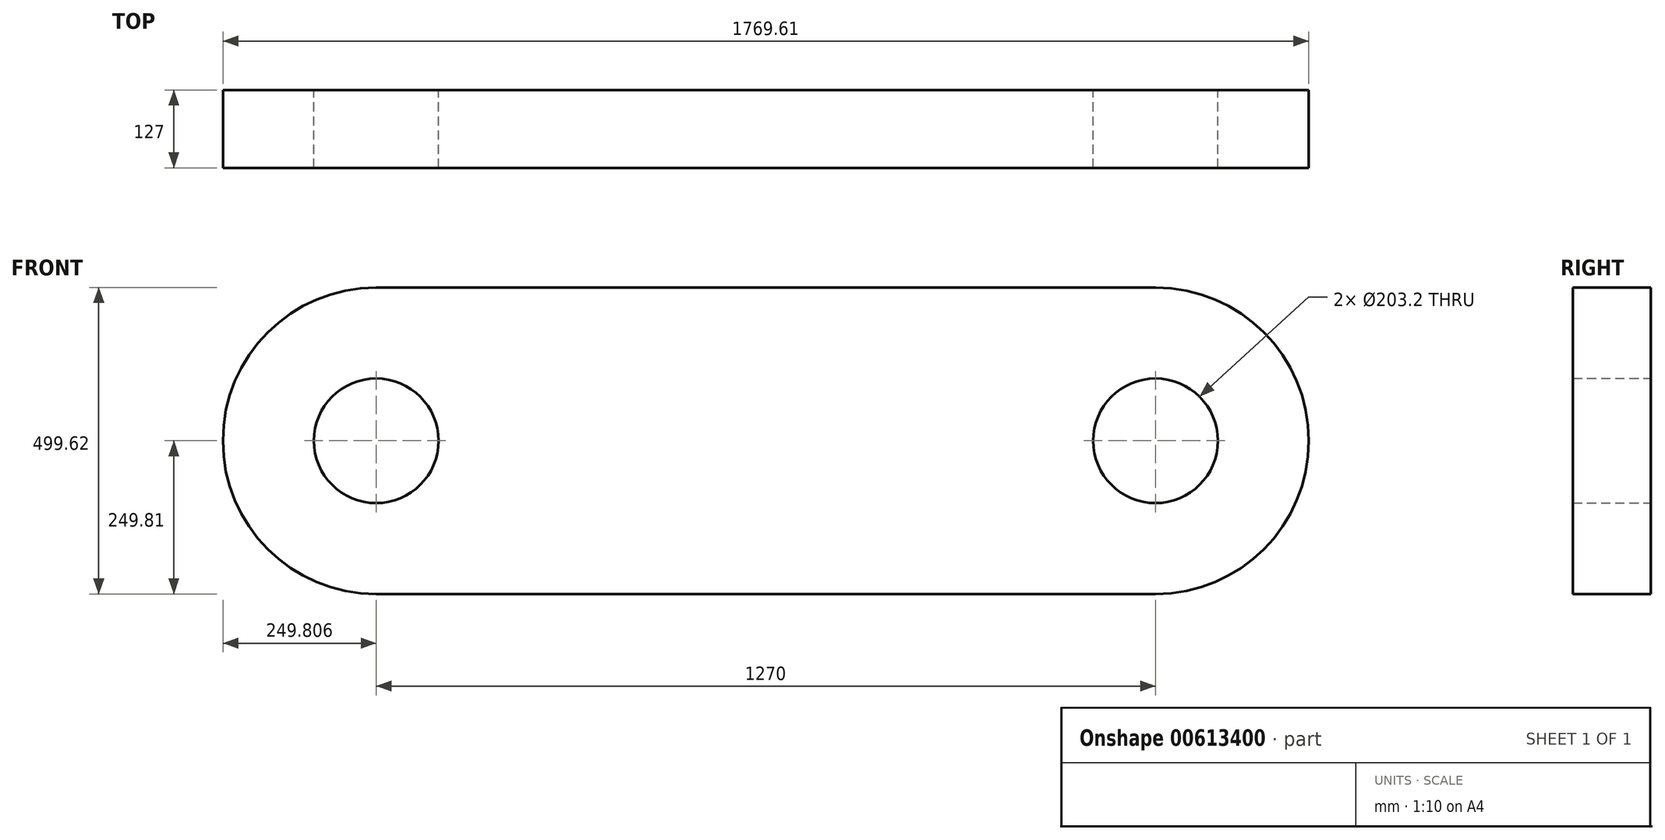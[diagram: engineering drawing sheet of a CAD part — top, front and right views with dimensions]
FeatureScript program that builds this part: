
annotation { "Feature Type Name" : "Feature", "Feature Type Description" : "" }
export const myFeature = defineFeature(function(context is Context, id is Id, definition is map)
    precondition{}
    {
        {
            var Q0;
            Q0=qCreatedBy(makeId("Front.planeOp"),FACE);
            var sketch = newSketch(context, id + "F0", { "sketchPlane" : qUnion([Q0])});
            skLineSegment(sketch, "E0", {"start": v(-559.22, 0) * mm, "end": v(710.78, 0) * mm});
            skCircle(sketch, "E1", {"center": v(-559.22, 0) * mm, "radius": 249.8 * mm});
            skCircle(sketch, "E2", {"center": v(710.78, 0) * mm, "radius": 249.8 * mm});
            skLineSegment(sketch, "E3", {"start": v(-559.22, 249.8) * mm, "end": v(710.78, 249.8) * mm});
            skLineSegment(sketch, "E4", {"start": v(-559.22, -249.8) * mm, "end": v(710.78, -249.8) * mm});
            skCircle(sketch, "E5", {"center": v(-559.22, 0) * mm, "radius": 101.6 * mm});
            skCircle(sketch, "E6", {"center": v(710.78, 0) * mm, "radius": 101.6 * mm});
            skSolve(sketch);
        }
        {
            var Q0;
            Q0=makeQuery(id+"F0.imprint","IMPRINT",FACE,{"disambiguationData":[TD([[makeQuery(id+"F0.imprint","IMPRINT",EDGE,{"derivedFrom":sQuery(id+"F0.wireOp",EDGE,"E5")}),-1.0]])]});
            var Q1;
            {var subQ5=sQuery(id+"F0.wireOp",EDGE,"E3");Q1=makeQuery(id+"F0.imprint","IMPRINT",FACE,{"disambiguationData":[TD([[makeQuery(id+"F0.imprint","IMPRINT",EDGE,{"derivedFrom":subQ5}),-1.0]])]});}
            var Q2;
            {var subQ5=sQuery(id+"F0.wireOp",EDGE,"E4");Q2=makeQuery(id+"F0.imprint","IMPRINT",FACE,{"disambiguationData":[TD([[makeQuery(id+"F0.imprint","IMPRINT",EDGE,{"derivedFrom":subQ5}),1.0]])]});}
            var Q3;
            Q3=makeQuery(id+"F0.imprint","IMPRINT",FACE,{"disambiguationData":[TD([[makeQuery(id+"F0.imprint","IMPRINT",EDGE,{"derivedFrom":sQuery(id+"F0.wireOp",EDGE,"E6")}),-1.0]])]});
            extrude(context, id + "F1", {"entities" : qUnion([Q0, Q1, Q2, Q3]), "depth" : 127 * mm, "offsetDistance" : 25.4 * mm});
        }
    });
